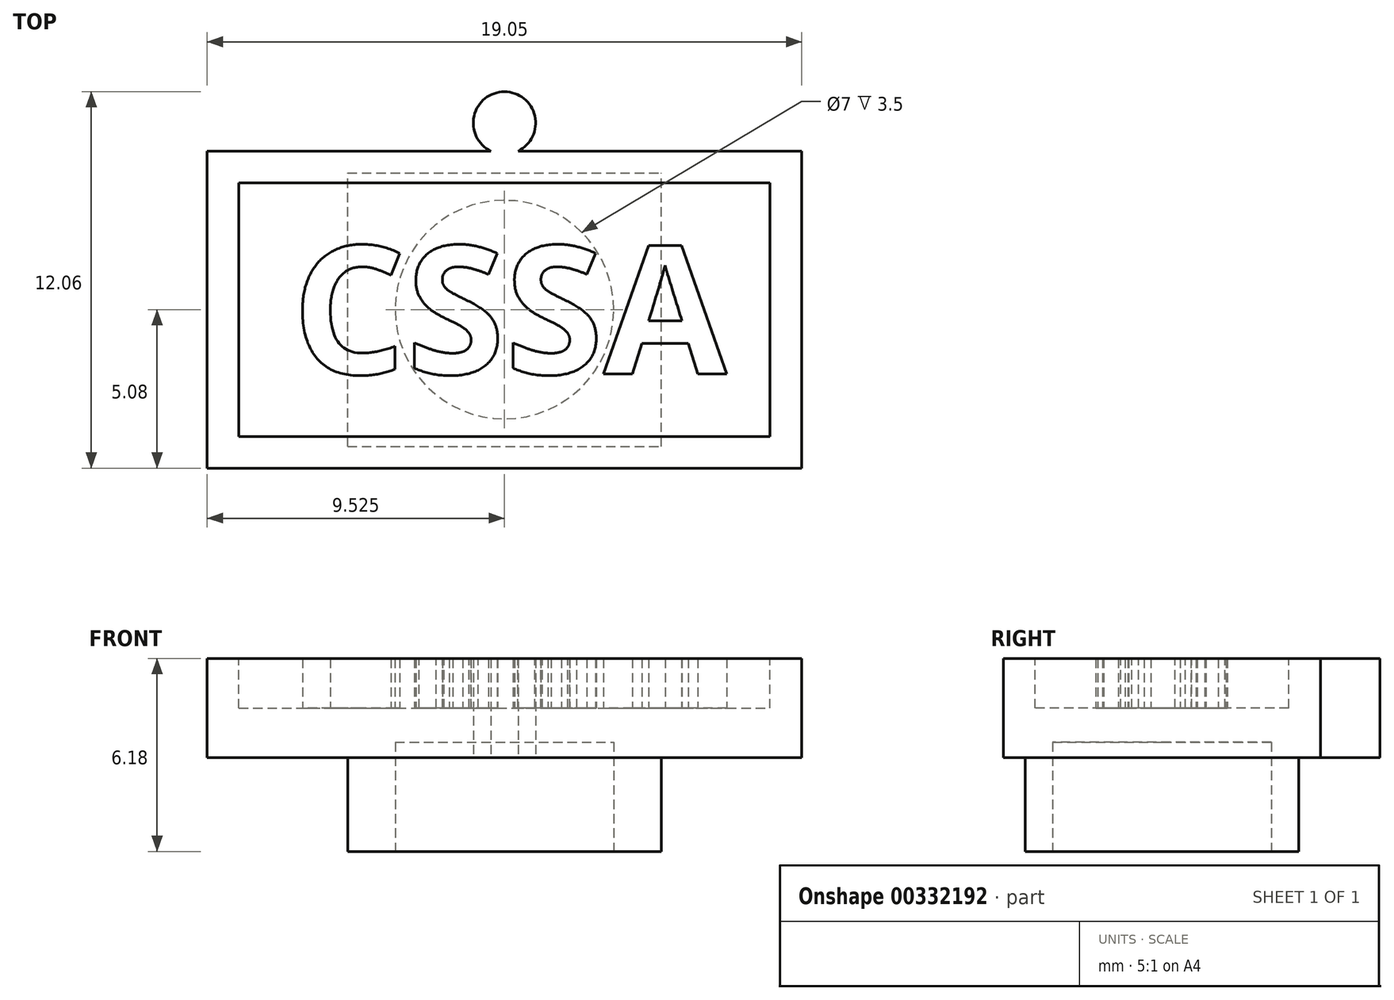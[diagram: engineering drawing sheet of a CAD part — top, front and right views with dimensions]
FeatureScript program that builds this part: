
annotation { "Feature Type Name" : "Feature", "Feature Type Description" : "" }
export const myFeature = defineFeature(function(context is Context, id is Id, definition is map)
    precondition{}
    {
        {
            var Q0;
            Q0=qCreatedBy(makeId("Top.planeOp"),FACE);
            var sketch = newSketch(context, id + "F0", { "sketchPlane" : qUnion([Q0])});
            skLineSegment(sketch, "E0.bottom", {"start": v(-19.05, 10.16) * mm, "end": v(0, 10.16) * mm});
            skLineSegment(sketch, "E0.top", {"start": v(-19.05, 0) * mm, "end": v(0, 0) * mm});
            skLineSegment(sketch, "E0.left", {"start": v(-19.05, 10.16) * mm, "end": v(-19.05, 0) * mm});
            skLineSegment(sketch, "E0.right", {"start": v(0, 10.16) * mm, "end": v(0, 0) * mm});
            skCircle(sketch, "E1", {"center": v(-9.53, 11.06) * mm, "radius": 1 * mm});
            skLineSegment(sketch, "E2", {"start": v(-9.52, 10.16) * mm, "end": v(-9.52, 0) * mm, "construction": true});
            skSolve(sketch);
        }
        {
            var Q0;
            Q0=qSketchRegion(id+"F0",true);
            extrude(context, id + "F1", {"entities" : qUnion([Q0]), "depth" : 3.17 * mm});
        }
        {
            var Q0;
            Q0=makeQuery(id+"F1.opExtrude","CAP_FACE",FACE,{"disambiguationData":[OSD([sQuery(id+"F0.wireOp",EDGE,"E0.bottom"),sQuery(id+"F0.wireOp",EDGE,"E0.top"),sQuery(id+"F0.wireOp",EDGE,"E0.left"),sQuery(id+"F0.wireOp",EDGE,"E0.right")])],"isStart":false});
            var sketch = newSketch(context, id + "F2", { "sketchPlane" : qUnion([Q0])});
            skLineSegment(sketch, "E3.bottom", {"start": v(-18.03, 9.14) * mm, "end": v(-1.02, 9.14) * mm});
            skLineSegment(sketch, "E3.top", {"start": v(-18.03, 1.02) * mm, "end": v(-1.02, 1.02) * mm});
            skLineSegment(sketch, "E3.left", {"start": v(-18.03, 9.14) * mm, "end": v(-18.03, 1.02) * mm});
            skLineSegment(sketch, "E3.right", {"start": v(-1.02, 9.14) * mm, "end": v(-1.02, 1.02) * mm});
            skSolve(sketch);
        }
        {
            var Q0;
            Q0=qSketchRegion(id+"F2",true);
            extrude(context, id + "F3", {"entities" : qUnion([Q0]), "operationType" : NewBodyOperationType.REMOVE, "oppositeDirection" : true, "depth" : 1.59 * mm});
        }
        {
            var Q0;
            Q0=makeQuery(id+"F1.opExtrude","CAP_FACE",FACE,{"disambiguationData":[OSD([sQuery(id+"F0.wireOp",EDGE,"E0.bottom"),sQuery(id+"F0.wireOp",EDGE,"E0.top"),sQuery(id+"F0.wireOp",EDGE,"E0.left"),sQuery(id+"F0.wireOp",EDGE,"E0.right"),sQuery(id+"F0.wireOp",EDGE,"E1"),sQuery(id+"F0.wireOp",EDGE,"25aa8db4-dd9b-41d2-b8c9-1594e9b75191"),sQuery(id+"F0.wireOp",EDGE,"40f63cb3-13d8-4821-a3c4-c05e674bd89b0.MirrorC")])],"isStart":true});
            var sketch = newSketch(context, id + "F4", { "sketchPlane" : qUnion([Q0])});
            skLineSegment(sketch, "E4.bottom", {"start": v(-14.55, -0.7) * mm, "end": v(-4.5, -0.7) * mm});
            skLineSegment(sketch, "E4.top", {"start": v(-14.55, -9.46) * mm, "end": v(-4.5, -9.46) * mm});
            skLineSegment(sketch, "E4.left", {"start": v(-14.55, -0.7) * mm, "end": v(-14.55, -9.46) * mm});
            skLineSegment(sketch, "E4.right", {"start": v(-4.5, -0.7) * mm, "end": v(-4.5, -9.46) * mm});
            skSolve(sketch);
        }
        {
            var Q0;
            Q0=qSketchRegion(id+"F4",true);
            extrude(context, id + "F5", {"entities" : qUnion([Q0]), "operationType" : NewBodyOperationType.ADD, "depth" : 3 * mm, "offsetDistance" : 25 * mm});
        }
        {
            var Q0;
            Q0=makeQuery(id+"F5.opExtrude","CAP_FACE",FACE,{"disambiguationData":[OSD([sQuery(id+"F4.wireOp",EDGE,"E4.bottom"),sQuery(id+"F4.wireOp",EDGE,"E4.top"),sQuery(id+"F4.wireOp",EDGE,"E4.left"),sQuery(id+"F4.wireOp",EDGE,"E4.right")])],"isStart":false});
            var sketch = newSketch(context, id + "F6", { "sketchPlane" : qUnion([Q0])});
            skCircle(sketch, "E5", {"center": v(-9.52, -5.08) * mm, "radius": 3.5 * mm});
            skLineSegment(sketch, "E6", {"start": v(-19.05, -5.08) * mm, "end": v(0, -5.08) * mm, "construction": true});
            skPoint(sketch, "E6.endSnap0", {"position": v(-4.5, -5.08) * mm});
            skLineSegment(sketch, "E7", {"start": v(-9.53, 0) * mm, "end": v(-9.53, -9.46) * mm, "construction": true});
            skSolve(sketch);
        }
        {
            var Q0;
            Q0=makeQuery(id+"F6.imprint","IMPRINT",FACE,{"disambiguationData":[TD([[makeQuery(id+"F6.imprint","IMPRINT",EDGE,{"derivedFrom":sQuery(id+"F6.wireOp",EDGE,"E5")}),1.0]])]});
            extrude(context, id + "F7", {"entities" : qUnion([Q0]), "operationType" : NewBodyOperationType.REMOVE, "oppositeDirection" : true, "depth" : 3.5 * mm, "offsetDistance" : 25 * mm});
        }
        {
            var Q0;
            Q0=makeQuery(id+"F3.boolean.opBoolean","COPY",FACE,{"derivedFrom":makeQuery(id+"F3.opExtrude","CAP_FACE",FACE,{"disambiguationData":[OSD([sQuery(id+"F2.wireOp",EDGE,"E3.bottom"),sQuery(id+"F2.wireOp",EDGE,"E3.top"),sQuery(id+"F2.wireOp",EDGE,"E3.left"),sQuery(id+"F2.wireOp",EDGE,"E3.right")])],"isStart":false})});
            var sketch = newSketch(context, id + "F8", { "sketchPlane" : qUnion([Q0])});
            skText(sketch, "E8", { "text": "CSSA", "fontName": "OpenSans-Bold.ttf"});
            const initialGuessF8  = {"E8": [-0.01633, 0.00302, 1, 0, 0.00413]};
            skSetInitialGuess(sketch, initialGuessF8);
            skSolve(sketch);
        }
        {
            var Q0;
            Q0=qSketchRegion(id+"F8",true);
            var Q1;
            Q1=makeQuery(id+"F1.opExtrude","CAP_FACE",FACE,{"disambiguationData":[OSD([sQuery(id+"F0.wireOp",EDGE,"E0.bottom"),sQuery(id+"F0.wireOp",EDGE,"E0.top"),sQuery(id+"F0.wireOp",EDGE,"E0.left"),sQuery(id+"F0.wireOp",EDGE,"E0.right"),sQuery(id+"F0.wireOp",EDGE,"E1")])],"isStart":false});
            extrude(context, id + "F9", {"entities" : qUnion([Q0]), "operationType" : NewBodyOperationType.ADD, "endBound" : BoundingType.UP_TO_SURFACE, "depth" : 25 * mm, "endBoundEntityFace" : qUnion([Q1]), "offsetDistance" : 25 * mm});
        }
    });
